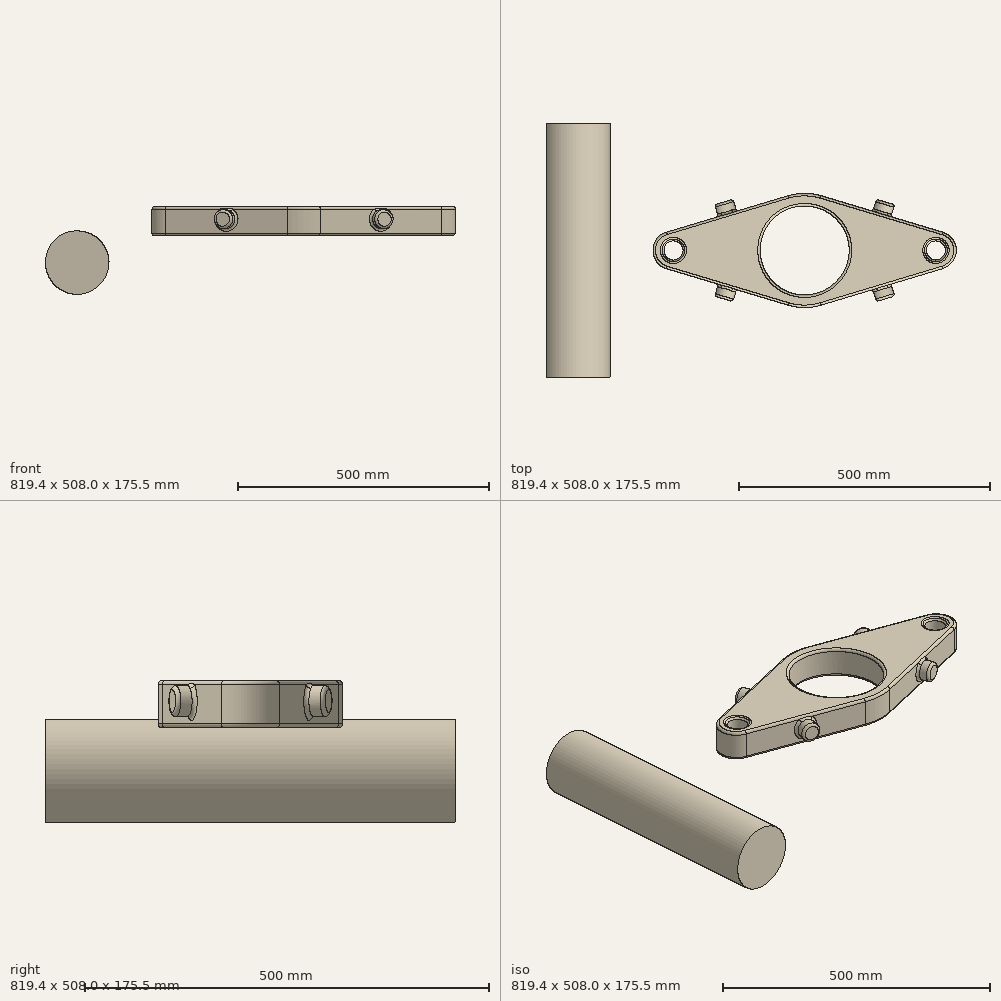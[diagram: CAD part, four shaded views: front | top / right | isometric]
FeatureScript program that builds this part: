
annotation { "Feature Type Name" : "Feature", "Feature Type Description" : "" }
export const myFeature = defineFeature(function(context is Context, id is Id, definition is map)
    precondition{}
    {
        {
            var Q0;
            Q0=qCreatedBy(makeId("Top.planeOp"),FACE);
            var sketch = newSketch(context, id + "F0", { "sketchPlane" : qUnion([Q0])});
            skCircle(sketch, "E0", {"center": v(0, 0) * mm, "radius": 114.3 * mm});
            skCircle(sketch, "E1", {"center": v(265.18, 0) * mm, "radius": 38.1 * mm});
            skLineSegment(sketch, "E2", {"start": v(32.84, 109.48) * mm, "end": v(276.13, 36.5) * mm});
            skLineSegment(sketch, "E3", {"start": v(32.84, -109.48) * mm, "end": v(276.13, -36.5) * mm});
            skCircle(sketch, "E4", {"center": v(0, 0) * mm, "radius": 88.9 * mm});
            skSolve(sketch);
        }
        {
            var Q0;
            Q0=makeQuery(id+"F0.imprint","IMPRINT",FACE,{"disambiguationData":[TD([[makeQuery(id+"F0.imprint","IMPRINT",EDGE,{"derivedFrom":sQuery(id+"F0.wireOp",EDGE,"E4")}),-1.0]])]});
            var Q1;
            {var subQ0=sQuery(id+"F0.wireOp",EDGE,"E2");Q1=makeQuery(id+"F0.imprint","IMPRINT",FACE,{"disambiguationData":[TD([[makeQuery(id+"F0.imprint","IMPRINT",EDGE,{"derivedFrom":subQ0}),-1.0]])]});}
            var Q2;
            {var subQ0=sQuery(id+"F0.wireOp",EDGE,"E1");var subQ1=makeQuery(id+"F0.imprint","INTERSECT",VERTEX,{"derivedFrom":[subQ0,sQuery(id+"F0.wireOp",EDGE,"E2")]});Q2=makeQuery(id+"F0.imprint","IMPRINT",FACE,{"disambiguationData":[TD([[makeQuery(id+"F0.imprint","IMPRINT",EDGE,{"disambiguationData":[TD([[subQ1,-1.0]])],"derivedFrom":subQ0}),1.0]])]});}
            extrude(context, id + "F1", {"entities" : qUnion([Q0, Q1, Q2]), "endBound" : BoundingType.SYMMETRIC, "depth" : 50.8 * mm, "offsetDistance" : 25.4 * mm});
        }
        {
            var Q0;
            Q0=makeQuery(id+"F1.opExtrude","SWEPT_FACE",FACE,{"disambiguationData":[OSD([sQuery(id+"F0.wireOp",EDGE,"E2")])]});
            var sketch = newSketch(context, id + "F2", { "sketchPlane" : qUnion([Q0])});
            skCircle(sketch, "E5", {"center": v(-127, 0) * mm, "radius": 19.05 * mm});
            skSolve(sketch);
        }
        {
            var Q0;
            Q0 = qSketchRegion(id + "F2", true);
            extrude(context, id + "F3", {"entities" : qUnion([Q0]), "operationType" : NewBodyOperationType.ADD, "endBound" : BoundingType.SYMMETRIC, "depth" : 49.78 * mm, "offsetDistance" : 25.4 * mm});
        }
        {
            var Q0;
            Q0=makeQuery(id+"F1.opExtrude","CAP_FACE",FACE,{"disambiguationData":[OSD([sQuery(id+"F0.wireOp",EDGE,"E0"),sQuery(id+"F0.wireOp",EDGE,"E1"),sQuery(id+"F0.wireOp",EDGE,"E2"),sQuery(id+"F0.wireOp",EDGE,"E3"),sQuery(id+"F0.wireOp",EDGE,"E4")])],"isStart":true});
            var sketch = newSketch(context, id + "F4", { "sketchPlane" : qUnion([Q0])});
            skLineSegment(sketch, "E6.bottom", {"start": v(228.6, 0) * mm, "end": v(127, 0) * mm});
            skLineSegment(sketch, "E6.top", {"start": v(228.6, 25.4) * mm, "end": v(127, 25.4) * mm});
            skLineSegment(sketch, "E6.left", {"start": v(127, 0) * mm, "end": v(127, 25.4) * mm});
            skLineSegment(sketch, "E6.right", {"start": v(228.6, 0) * mm, "end": v(228.6, 25.4) * mm});
            skSolve(sketch);
        }
        {
            var Q0;
            Q0 = qSketchRegion(id + "F4", true);
            var Q1;
            Q1=makeQuery(id+"F4.imprint","IMPRINT",FACE,{"disambiguationData":[TD([[makeQuery(id+"F4.imprint","IMPRINT",EDGE,{"derivedFrom":sQuery(id+"F4.wireOp",EDGE,"E6.bottom")}),1.0]])]});
            extrude(context, id + "F5", {"entities" : qUnion([Q0, Q1]), "operationType" : NewBodyOperationType.ADD, "depth" : 7.62 * mm, "offsetDistance" : 25.4 * mm});
        }
        {
            var Q0;
            Q0=makeQuery(id+"F5.opExtrude","CAP_FACE",FACE,{"disambiguationData":[OSD([sQuery(id+"F0.wireOp",EDGE,"E0"),sQuery(id+"F0.wireOp",EDGE,"E1"),sQuery(id+"F0.wireOp",EDGE,"E2"),sQuery(id+"F0.wireOp",EDGE,"E3"),sQuery(id+"F0.wireOp",EDGE,"E4")])],"isStart":false});
            var sketch = newSketch(context, id + "F6", { "sketchPlane" : qUnion([Q0])});
            skCircle(sketch, "E7", {"center": v(262.27, 0) * mm, "radius": 19.05 * mm});
            skPoint(sketch, "E7.centerSnap0", {"position": v(303.28, 0) * mm});
            skSolve(sketch);
        }
        {
            var Q0;
            Q0 = qSketchRegion(id + "F6", true);
            extrude(context, id + "F7", {"entities" : qUnion([Q0]), "operationType" : NewBodyOperationType.REMOVE, "endBound" : BoundingType.THROUGH_ALL, "oppositeDirection" : true, "depth" : 25.4 * mm, "offsetDistance" : 25.4 * mm});
        }
        {
            var Q0;
            Q0=makeQuery(id+"F7.boolean.opBoolean","COPY",FACE,{"derivedFrom":makeQuery(id+"F7.opExtrude","SWEPT_FACE",FACE,{"disambiguationData":[OSD([sQuery(id+"F6.wireOp",EDGE,"E7")])]})});
            chamfer(context, id + "F8", {"entities" : qUnion([Q0]), "width" : 5.08 * mm, "tangentPropagation" : true});
        }
        {
            var Q0;
            Q0=makeQuery(id+"F5.opExtrude","CAP_FACE",FACE,{"disambiguationData":[OSD([sQuery(id+"F0.wireOp",EDGE,"E0"),sQuery(id+"F0.wireOp",EDGE,"E1"),sQuery(id+"F0.wireOp",EDGE,"E2"),sQuery(id+"F0.wireOp",EDGE,"E3"),sQuery(id+"F0.wireOp",EDGE,"E4")])],"isStart":false});
            fillet(context, id + "F9", {"entities" : qUnion([Q0]), "radius" : 5.08 * mm, "tangentPropagation" : true, "allowEdgeOverflow" : false});
        }
        {
            var Q0;
            Q0=makeQuery(id+"F1.opExtrude","CAP_FACE",FACE,{"disambiguationData":[OSD([sQuery(id+"F0.wireOp",EDGE,"E0"),sQuery(id+"F0.wireOp",EDGE,"E1"),sQuery(id+"F0.wireOp",EDGE,"E2"),sQuery(id+"F0.wireOp",EDGE,"E3"),sQuery(id+"F0.wireOp",EDGE,"E4")])],"isStart":false});
            fillet(context, id + "F10", {"entities" : qUnion([Q0]), "radius" : 5.08 * mm, "tangentPropagation" : true, "allowEdgeOverflow" : false});
        }
        {
            var Q0;
            Q0=makeQuery(id+"F3.opExtrude","CAP_EDGE",EDGE,{"disambiguationData":[OSD([sQuery(id+"F2.wireOp",EDGE,"E5")])],"isStart":false});
            var Q1;
            Q1=makeQuery(id+"F3.boolean.opBoolean","INTERSECT",EDGE,{"derivedFrom":[makeQuery(id+"F1.opExtrude","SWEPT_FACE",FACE,{"disambiguationData":[OSD([sQuery(id+"F0.wireOp",EDGE,"E2")])]}),makeQuery(id+"F3.opExtrude","SWEPT_FACE",FACE,{"disambiguationData":[OSD([sQuery(id+"F2.wireOp",EDGE,"E5")])]})]});
            fillet(context, id + "F11", {"entities" : qUnion([Q0, Q1]), "radius" : 5.08 * mm, "tangentPropagation" : true, "allowEdgeOverflow" : false});
        }
        {
            var Q0;
            Q0=makeQuery(id+"F5.opExtrude","CAP_FACE",FACE,{"disambiguationData":[OSD([sQuery(id+"F0.wireOp",EDGE,"E0"),sQuery(id+"F0.wireOp",EDGE,"E1"),sQuery(id+"F0.wireOp",EDGE,"E2"),sQuery(id+"F0.wireOp",EDGE,"E3"),sQuery(id+"F0.wireOp",EDGE,"E4")])],"isStart":false});
            shell(context, id + "F12", {"entities" : qUnion([Q0]), "thickness" : 2.54 * mm});
        }
        {
            var Q0;
            Q0=makeQuery(id+"F1.opExtrude","SWEPT_BODY",BODY,{"disambiguationData":[OSD([sQuery(id+"F0.wireOp",EDGE,"E0"),sQuery(id+"F0.wireOp",EDGE,"E1"),sQuery(id+"F0.wireOp",EDGE,"E2"),sQuery(id+"F0.wireOp",EDGE,"E3"),sQuery(id+"F0.wireOp",EDGE,"E4")])]});
            var Q1;
            Q1=qCreatedBy(makeId("Front.planeOp"),FACE);
            mirror(context, id + "F13", {"operationType" : NewBodyOperationType.ADD, "entities" : qUnion([Q0]), "mirrorPlane" : qUnion([Q1])});
        }
        {
            var Q0;
            Q0=makeQuery(id+"F1.opExtrude","SWEPT_BODY",BODY,{"disambiguationData":[OSD([sQuery(id+"F0.wireOp",EDGE,"E0"),sQuery(id+"F0.wireOp",EDGE,"E1"),sQuery(id+"F0.wireOp",EDGE,"E2"),sQuery(id+"F0.wireOp",EDGE,"E3"),sQuery(id+"F0.wireOp",EDGE,"E4")])]});
            var Q1;
            Q1=qCreatedBy(makeId("Right.planeOp"),FACE);
            mirror(context, id + "F14", {"operationType" : NewBodyOperationType.ADD, "entities" : qUnion([Q0]), "mirrorPlane" : qUnion([Q1])});
        }
        {
            var Q0;
            Q0=qCreatedBy(makeId("Front.planeOp"),FACE);
            var sketch = newSketch(context, id + "F15", { "sketchPlane" : qUnion([Q0])});
            skCircle(sketch, "E8", {"center": v(-452.64, -86.57) * mm, "radius": 63.5 * mm});
            skSolve(sketch);
        }
        {
            var Q0;
            Q0=makeQuery(id+"F15.imprint","IMPRINT",FACE,{"disambiguationData":[TD([[makeQuery(id+"F15.imprint","IMPRINT",EDGE,{"derivedFrom":sQuery(id+"F15.wireOp",EDGE,"E8")}),1.0]])]});
            extrude(context, id + "F16", {"entities" : qUnion([Q0]), "operationType" : NewBodyOperationType.ADD, "endBound" : BoundingType.SYMMETRIC, "depth" : 508 * mm, "offsetDistance" : 25.4 * mm});
        }
    });
